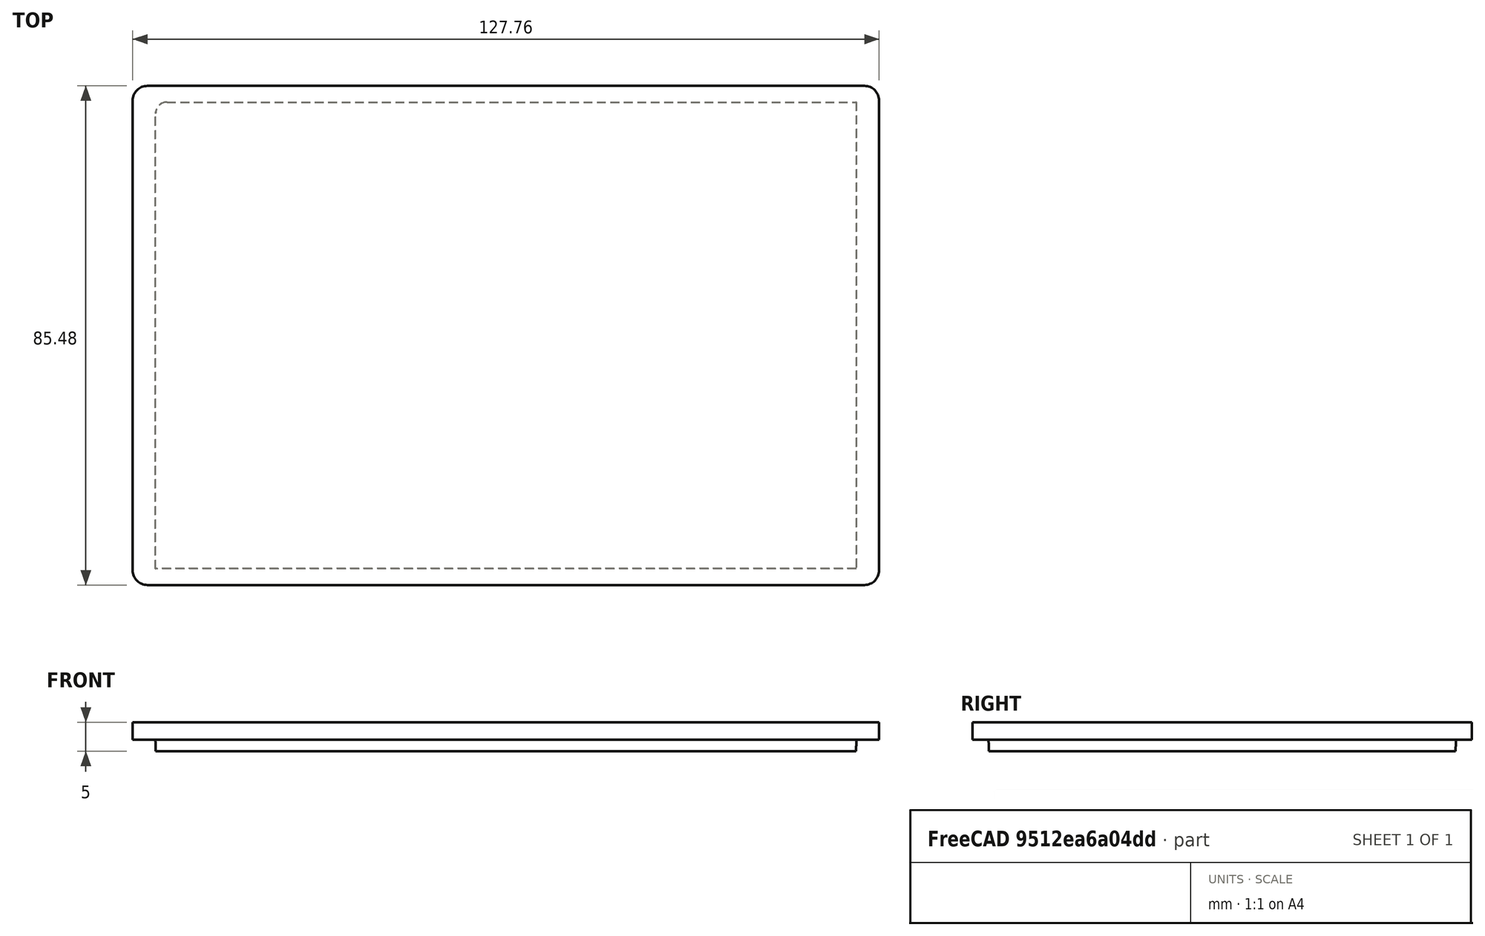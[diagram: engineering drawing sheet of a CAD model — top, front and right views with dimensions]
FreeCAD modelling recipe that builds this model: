
FCSTD DOCUMENT  (FreeCAD 0.20R29410 (Git))
Label: racklid_2mm_v1
License: All rights reserved
LicenseURL: http://en.wikipedia.org/wiki/All_rights_reserved
objects: Sketcher::SketchObject×2, PartDesign::Pad×2, PartDesign::Body×1, Mesh::Feature×1
note: 7 computed .brp shape members not serialized (recipe doc carries the construction recipe); baked Part::Feature solids carry a one-line shape summary decoded from their .brp

FEATURE [Sketcher::SketchObject] Sketch  label="BasePlate"
  FullyConstrained = true
  MapMode = 5
  Support = -> [XY_Plane]
  sketch-geometry (8):
    g0: LineSegment StartX=-61.38 StartY=-42.74 StartZ=0 EndX=61.38 EndY=-42.74 EndZ=0
    g1: LineSegment StartX=63.88 StartY=-40.24 StartZ=0 EndX=63.88 EndY=40.24 EndZ=0
    g2: LineSegment StartX=61.38 StartY=42.74 StartZ=0 EndX=-61.38 EndY=42.74 EndZ=0
    g3: LineSegment StartX=-63.88 StartY=40.24 StartZ=0 EndX=-63.88 EndY=-40.24 EndZ=0
    g4: ArcOfCircle CenterX=-61.38 CenterY=-40.24 CenterZ=0 NormalX=0 NormalY=0 NormalZ=1 AngleXU=0 Radius=2.5 StartAngle=3.14159 EndAngle=4.71239
    g5: ArcOfCircle CenterX=61.38 CenterY=-40.24 CenterZ=0 NormalX=0 NormalY=0 NormalZ=1 AngleXU=0 Radius=2.5 StartAngle=4.71239 EndAngle=6.28319
    g6: ArcOfCircle CenterX=61.38 CenterY=40.24 CenterZ=0 NormalX=0 NormalY=0 NormalZ=1 AngleXU=0 Radius=2.5 StartAngle=1.3e-15 EndAngle=1.5708
    g7: ArcOfCircle CenterX=-61.38 CenterY=40.24 CenterZ=0 NormalX=0 NormalY=0 NormalZ=1 AngleXU=0 Radius=2.5 StartAngle=1.5708 EndAngle=3.14159
  constraints (20):
    c: Horizontal(g0)
    c: Horizontal(g2)
    c: Vertical(g1)
    c: Vertical(g3)
    c: Tangent(g3,g4) = -1.5708
    c: Tangent(g0,g4) = -1.5708
    c: Tangent(g0,g5) = -1.5708
    c: Tangent(g1,g5) = -1.5708
    c: Tangent(g1,g6) = -1.5708
    c: Tangent(g2,g6) = -1.5708
    c: Tangent(g2,g7) = -1.5708
    c: Tangent(g3,g7) = -1.5708
    c: Radius(g4) = 2.5
    c: DistanceX(g-1,g3) = -63.88
    c: DistanceY(g0,g-1) = 42.74
    c: Radius(g7) = 2.5
    c: Radius(g6) = 2.5
    c: Radius(g5) = 2.5
    c: DistanceY(g0,g2) = 85.48
    c: DistanceX(g3,g1) = 127.76
FEATURE [PartDesign::Pad] Pad
  Direction = (0,0,1)
  Length = 3
  Length2 = 2
  Profile = -> Sketch
  ReferenceAxis = -> Sketch [N_Axis]
  Type = 0
FEATURE [Sketcher::SketchObject] Sketch001  label="BottomFrame"
  FullyConstrained = true
  MapMode = 2
  Support = -> [Pad]
  sketch-geometry (5):
    g0: LineSegment StartX=-58 StartY=40 StartZ=0 EndX=60 EndY=40 EndZ=0
    g1: LineSegment StartX=60 StartY=40 StartZ=0 EndX=60 EndY=-40 EndZ=0
    g2: LineSegment StartX=60 StartY=-40 StartZ=0 EndX=-60 EndY=-40 EndZ=0
    g3: LineSegment StartX=-60 StartY=-40 StartZ=0 EndX=-60 EndY=38 EndZ=0
    g4: ArcOfCircle CenterX=-58 CenterY=38 CenterZ=0 NormalX=0 NormalY=0 NormalZ=1 AngleXU=0 Radius=2 StartAngle=1.5708 EndAngle=3.14159
  constraints (14):
    c: Coincident(g0,g1)
    c: Coincident(g1,g2)
    c: Coincident(g2,g3)
    c: Horizontal(g0)
    c: Horizontal(g2)
    c: Vertical(g1)
    c: Vertical(g3)
    c: DistanceX(g2,g-1) = 60
    c: DistanceX(g2,g1) = 120
    c: DistanceY(g1,g0) = 80
    c: DistanceY(g1,g-1) = 40
    c: Tangent(g3,g4) = 1.5708
    c: Tangent(g0,g4) = 1.5708
    c: Radius(g4) = 2
FEATURE [PartDesign::Pad] Pad001
  BaseFeature = -> Pad
  Direction = (0,0,1)
  Length = 2
  Length2 = 10
  Profile = -> Sketch001
  ReferenceAxis = -> Sketch001 [N_Axis]
  Reversed = true
  TaperAngle = -2
  Type = 0
FEATURE [PartDesign::Body] Body
  Group = -> [Sketch,Pad,Sketch001,Pad001]
  Origin = -> Origin
  Tip = -> Pad001
FEATURE [Mesh::Feature] Mesh  label="Body (Meshed)"
